FREECAD ASSEMBLY — COMPONENT RECIPES ("gripper-assembly")

This assembly document has 15 components, labeled P0..P14 below (a component is one placed body or linked part). 0 of them carry a construction recipe — the FreeCAD feature program that regenerates the part from scratch, quoted from this document or its linked companion documents; the rest are supplied as boundary geometry only. No exploded tour is included for this assembly.
COMPONENT P0 — geometry summary ("Body079 (Mirror #6)"; no construction recipe available for this part):
  bounding box: 68.9 x 37.7 x 6.0 mm
  tessellated surface: 5,058 triangles
  volume: 2788 mm^3 (18% of its bounding box)
COMPONENT P1 — geometry summary ("Body080 (Mirror #7)"; no construction recipe available for this part):
  bounding box: 62.7 x 15.0 x 4.0 mm
  tessellated surface: 5,028 triangles
  volume: 2237 mm^3 (59% of its bounding box)
COMPONENT P2 — geometry summary ("Clone004 (Mirror #5)"; no construction recipe available for this part):
  bounding box: 41.6 x 39.8 x 6.0 mm
  tessellated surface: 3,652 triangles
  volume: 2105 mm^3 (21% of its bounding box)
COMPONENT P3 — geometry summary ("Corps"; no construction recipe available for this part):
  bounding box: 44.0 x 17.0 x 13.0 mm
  tessellated surface: 3,136 triangles
  volume: 3711 mm^3 (38% of its bounding box)
  symmetry: 2-fold rotationally symmetric about the y axis; mirror-symmetric across its x mid-plane, z mid-plane
COMPONENT P4 — geometry summary ("Corps002"; no construction recipe available for this part):
  bounding box: 41.6 x 39.8 x 6.0 mm
  tessellated surface: 3,652 triangles
  volume: 2105 mm^3 (21% of its bounding box)
COMPONENT P5 — geometry summary ("Corps003"; no construction recipe available for this part):
  bounding box: 68.9 x 37.7 x 6.0 mm
  tessellated surface: 5,058 triangles
  volume: 2788 mm^3 (18% of its bounding box)
COMPONENT P6 — geometry summary ("Corps005"; no construction recipe available for this part):
  bounding box: 77.7 x 60.0 x 37.7 mm
  tessellated surface: 10,780 triangles
  volume: 26861 mm^3 (15% of its bounding box)
COMPONENT P7 — geometry summary ("Corps007"; no construction recipe available for this part):
  bounding box: 90.0 x 71.9 x 55.0 mm
  tessellated surface: 11,758 triangles
  volume: 103224 mm^3 (29% of its bounding box)
COMPONENT P8 — geometry summary ("Corps008"; no construction recipe available for this part):
  bounding box: 55.8 x 36.7 x 4.0 mm
  tessellated surface: 6,048 triangles
  volume: 3499 mm^3 (43% of its bounding box)
COMPONENT P9 — geometry summary ("Corps010"; no construction recipe available for this part):
  bounding box: 52.0 x 18.5 x 11.4 mm
  tessellated surface: 3,760 triangles
  volume: 6647 mm^3 (60% of its bounding box)
  symmetry: mirror-symmetric across its x mid-plane
COMPONENT P10 — geometry summary ("Corps011"; no construction recipe available for this part):
  bounding box: 224.4 x 105.0 x 13.2 mm
  tessellated surface: 14,676 triangles
  volume: 69376 mm^3 (22% of its bounding box)
  symmetry: mirror-symmetric across its x mid-plane
COMPONENT P11 — geometry summary ("MG996"; no construction recipe available for this part):
  bounding box: 62.0 x 46.0 x 20.1 mm
  tessellated surface: 8,740 triangles
  volume: 32582 mm^3 (57% of its bounding box)
  symmetry: mirror-symmetric across its z mid-plane
COMPONENT P12 — geometry summary ("Palonnier"; no construction recipe available for this part):
  bounding box: 62.7 x 15.0 x 4.0 mm
  tessellated surface: 4,146 triangles
  volume: 2268 mm^3 (60% of its bounding box)
COMPONENT P13 — geometry summary ("SupportServoGripper"; no construction recipe available for this part):
  bounding box: 60.0 x 42.5 x 41.4 mm
  tessellated surface: 10,812 triangles
  volume: 14571 mm^3 (14% of its bounding box)
  symmetry: mirror-symmetric across its x mid-plane
COMPONENT P14 — geometry summary ("SupportServoPivot"; no construction recipe available for this part):
  bounding box: 56.9 x 42.8 x 18.5 mm
  tessellated surface: 4,800 triangles
  volume: 13025 mm^3 (29% of its bounding box)
PROVENANCE & LICENSES
A FreeCAD (.FCStd) document from a public repository crawl; recipes are the document's own serialized feature recipes (and, for linked parts, companion documents' recipes).
License: as declared in the source repository (recorded in the dataset sidecar).
